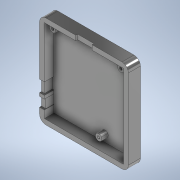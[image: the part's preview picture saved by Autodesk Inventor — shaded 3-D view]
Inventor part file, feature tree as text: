
AUTODESK INVENTOR PART (.ipt)
format: ipt  version: 2021 (Build 250183000, 183)  size: 186,880 bytes
history: native  units: mm
features: extrude x5, sketch x4, plane x1, fillet x1
ambient origin geometry x8: Origin, YZ Plane, XZ Plane, XY Plane, X Axis, Y Axis, Z Axis, Center Point
bodies: Solid1 (feature_tree)
feature tree (11):
  sketch  "Sketch1"  dims[d0=2.0mm d1=4.0mm]
  extrude  "Extrusion1"  Depth=4.0mm
  extrude  "Extrusion2"  Depth=3.0mm TaperAngle=0.0deg
  extrude  "Extrusion4"  Depth=8.0mm
  plane  "Work Plane1"
  extrude  "Extrusion5"  Depth=8.0mm TaperAngle=0.0deg
  fillet  "Fillet1"  [1 undecoded]
  extrude  "Extrusion6"  Depth=8.0mm TaperAngle=0.0deg
  sketch  "Sketch2"  dims[d2=15.0mm d3=0.0mm d4=3.0mm d5=0.0mm]
  sketch  "Sketch3"  dims[d8=8.0mm d9=8.0mm]
  sketch  "Sketch4"  dims[d10=8.0mm d11=8.0mm d12=0.0mm d13=-12.662mm d14=8.0mm d15=0.0mm d16=8.0mm d17=8.0mm d18=0.0mm]
note: 1 required parameter value undecoded (feature->parameter linkage not recoverable at this tier; creation-order binding heuristic only, values carry confidence <= 0.55)
